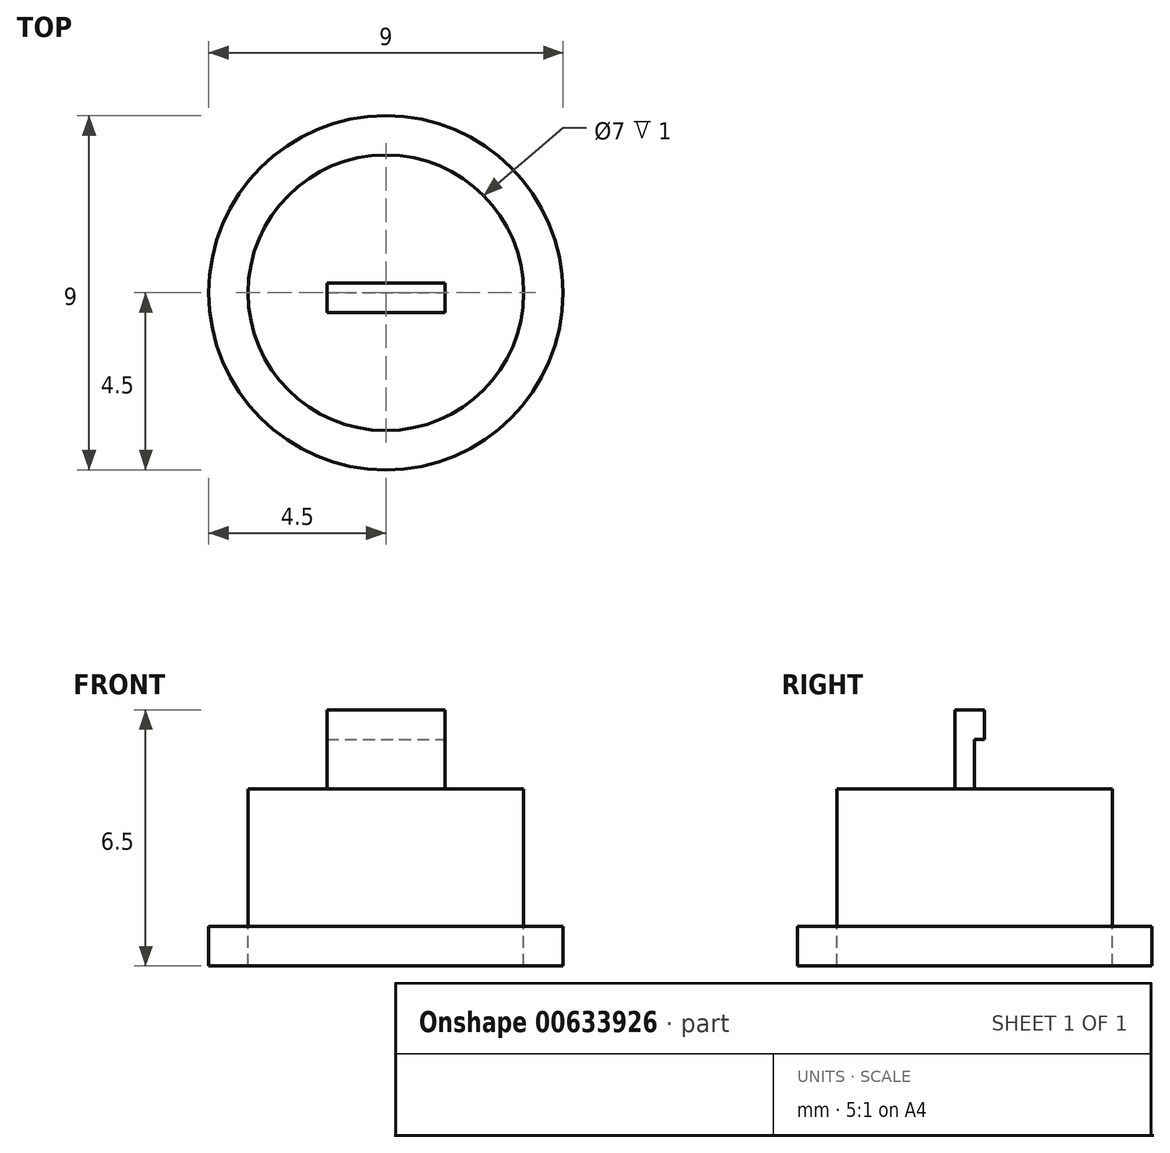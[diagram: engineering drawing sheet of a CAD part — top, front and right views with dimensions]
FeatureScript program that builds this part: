
annotation { "Feature Type Name" : "Feature", "Feature Type Description" : "" }
export const myFeature = defineFeature(function(context is Context, id is Id, definition is map)
    precondition{}
    {
        {
            var Q0;
            Q0=qCreatedBy(makeId("Top.planeOp"),FACE);
            var sketch = newSketch(context, id + "F0", { "sketchPlane" : qUnion([Q0])});
            skCircle(sketch, "E0", {"center": v(0, 0) * mm, "radius": 3.5 * mm});
            skSolve(sketch);
        }
        {
            var Q0;
            Q0=makeQuery(id+"F0.imprint","IMPRINT",FACE,{"disambiguationData":[TD([[makeQuery(id+"F0.imprint","IMPRINT",EDGE,{"derivedFrom":sQuery(id+"F0.wireOp",EDGE,"E0")}),1.0]])]});
            extrude(context, id + "F1", {"entities" : qUnion([Q0]), "depth" : 3.5 * mm, "offsetDistance" : 25.4 * mm});
        }
        {
            var Q0;
            Q0=makeQuery(id+"F1.opExtrude","CAP_FACE",FACE,{"disambiguationData":[OSD([sQuery(id+"F0.wireOp",EDGE,"E0")])],"isStart":true});
            var sketch = newSketch(context, id + "F2", { "sketchPlane" : qUnion([Q0])});
            skCircle(sketch, "E1", {"center": v(0, 0) * mm, "radius": 4.5 * mm});
            skSolve(sketch);
        }
        {
            var Q0;
            Q0=makeQuery(id+"F2.imprint","IMPRINT",FACE,{"disambiguationData":[TD([[makeQuery(id+"F2.imprint","IMPRINT",EDGE,{"derivedFrom":sQuery(id+"F2.wireOp",EDGE,"E1")}),1.0]])]});
            extrude(context, id + "F3", {"entities" : qUnion([Q0]), "depth" : 1 * mm, "offsetDistance" : 25.4 * mm});
        }
        {
            var Q0;
            Q0=makeQuery(id+"F1.opExtrude","CAP_FACE",FACE,{"disambiguationData":[OSD([sQuery(id+"F0.wireOp",EDGE,"E0")])],"isStart":true});
            var sketch = newSketch(context, id + "F4", { "sketchPlane" : qUnion([Q0])});
            skCircle(sketch, "E2", {"center": v(0, 0) * mm, "radius": 3.5 * mm});
            skSolve(sketch);
        }
        {
            var Q0;
            Q0=makeQuery(id+"F4.imprint","IMPRINT",FACE,{"disambiguationData":[TD([[makeQuery(id+"F4.imprint","IMPRINT",EDGE,{"derivedFrom":sQuery(id+"F4.wireOp",EDGE,"E2")}),-1.0]])]});
            extrude(context, id + "F5", {"entities" : qUnion([Q0]), "depth" : 1 * mm, "offsetDistance" : 25.4 * mm});
        }
        {
            var Q0;
            Q0=makeQuery(id+"F1.opExtrude","CAP_FACE",FACE,{"disambiguationData":[OSD([sQuery(id+"F0.wireOp",EDGE,"E0")])],"isStart":false});
            var sketch = newSketch(context, id + "F6", { "sketchPlane" : qUnion([Q0])});
            skLineSegment(sketch, "E3.bottom", {"start": v(-1.5, 1.5) * mm, "end": v(1.5, 1.5) * mm});
            skLineSegment(sketch, "E3.top", {"start": v(-1.5, -1.5) * mm, "end": v(1.5, -1.5) * mm});
            skLineSegment(sketch, "E3.left", {"start": v(-1.5, 1.5) * mm, "end": v(-1.5, -1.5) * mm});
            skLineSegment(sketch, "E3.right", {"start": v(1.5, 1.5) * mm, "end": v(1.5, -1.5) * mm});
            skSolve(sketch);
        }
        {
            var Q0;
            Q0=makeQuery(id+"F6.imprint","IMPRINT",FACE,{"disambiguationData":[TD([[makeQuery(id+"F6.imprint","IMPRINT",EDGE,{"derivedFrom":sQuery(id+"F6.wireOp",EDGE,"E3.bottom")}),-1.0]])]});
            extrude(context, id + "F7", {"entities" : qUnion([Q0]), "operationType" : NewBodyOperationType.ADD, "depth" : 2 * mm, "offsetDistance" : 25.4 * mm});
        }
        {
            var Q0;
            Q0=makeQuery(id+"F7.opExtrude","SWEPT_FACE",FACE,{"disambiguationData":[OSD([sQuery(id+"F6.wireOp",EDGE,"E3.right")])]});
            var sketch = newSketch(context, id + "F8", { "sketchPlane" : qUnion([Q0])});
            skPoint(sketch, "E4.endSnap0", {"position": v(0, 5.5) * mm});
            skLineSegment(sketch, "E5.bottom", {"start": v(-0.5, 3.5) * mm, "end": v(0.25, 3.5) * mm});
            skLineSegment(sketch, "E5.top", {"start": v(-0.5, 5.5) * mm, "end": v(0.25, 5.5) * mm});
            skLineSegment(sketch, "E5.left", {"start": v(-0.5, 3.5) * mm, "end": v(-0.5, 5.5) * mm});
            skLineSegment(sketch, "E5.right", {"start": v(0.25, 3.5) * mm, "end": v(0.25, 5.5) * mm});
            skLineSegment(sketch, "E6", {"start": v(0, 5.5) * mm, "end": v(0, 3.5) * mm});
            skLineSegment(sketch, "E7", {"start": v(0, 5.5) * mm, "end": v(0, 4.75) * mm});
            skLineSegment(sketch, "E8", {"start": v(0, 4.75) * mm, "end": v(0.25, 4.75) * mm});
            skLineSegment(sketch, "E9", {"start": v(0.25, 4.75) * mm, "end": v(-0.5, 5.5) * mm});
            skLineSegment(sketch, "E10", {"start": v(0, 4.75) * mm, "end": v(0, 3.5) * mm});
            skSolve(sketch);
        }
        {
            var Q0;
            {var subQ4=sQuery(id+"F8.wireOp",EDGE,"E8");Q0=makeQuery(id+"F8.imprint","IMPRINT",FACE,{"disambiguationData":[TD([[makeQuery(id+"F8.imprint","IMPRINT",EDGE,{"derivedFrom":subQ4}),-1.0]])]});}
            var Q1;
            {var subQ1=sQuery(id+"F8.wireOp",EDGE,"E5.top");var subQ3=sQuery(id+"F8.wireOp",EDGE,"E7");var subQ4=makeQuery(id+"F8.imprint","INTERSECT",VERTEX,{"derivedFrom":[subQ1,subQ3]});Q1=makeQuery(id+"F8.imprint","IMPRINT",FACE,{"disambiguationData":[TD([[makeQuery(id+"F8.imprint","IMPRINT",EDGE,{"disambiguationData":[TD([[subQ4,-1.0]])],"derivedFrom":subQ3}),1.0]])]});}
            var Q2;
            {var subQ1=sQuery(id+"F8.wireOp",EDGE,"E5.top");var subQ3=sQuery(id+"F8.wireOp",EDGE,"E7");var subQ4=makeQuery(id+"F8.imprint","INTERSECT",VERTEX,{"derivedFrom":[subQ1,subQ3]});Q2=makeQuery(id+"F8.imprint","IMPRINT",FACE,{"disambiguationData":[TD([[makeQuery(id+"F8.imprint","IMPRINT",EDGE,{"disambiguationData":[TD([[subQ4,-1.0]])],"derivedFrom":subQ3}),-1.0]])]});}
            var Q3;
            {var subQ0=sQuery(id+"F8.wireOp",EDGE,"E5.left");Q3=makeQuery(id+"F8.imprint","IMPRINT",FACE,{"disambiguationData":[TD([[makeQuery(id+"F8.imprint","IMPRINT",EDGE,{"derivedFrom":subQ0}),1.0]])]});}
            var Q4;
            {var subQ0=sQuery(id+"F6.wireOp",EDGE,"E3.right");var subQ1=makeQuery(id+"F7.opExtrude","SWEPT_EDGE",EDGE,{"disambiguationData":[OSD([sQuery(id+"F6.wireOp",EDGE,"E3.bottom"),subQ0])]});Q4=makeQuery(id+"F8.imprint","IMPRINT",FACE,{"disambiguationData":[TD([[makeQuery(id+"F8.imprint","IMPRINT",EDGE,{"derivedFrom":subQ1}),-1.0]])]});}
            extrude(context, id + "F9", {"entities" : qUnion([Q0, Q1, Q2, Q3, Q4]), "operationType" : NewBodyOperationType.REMOVE, "oppositeDirection" : true, "depth" : 25.4 * mm, "offsetDistance" : 25.4 * mm});
        }
    });
